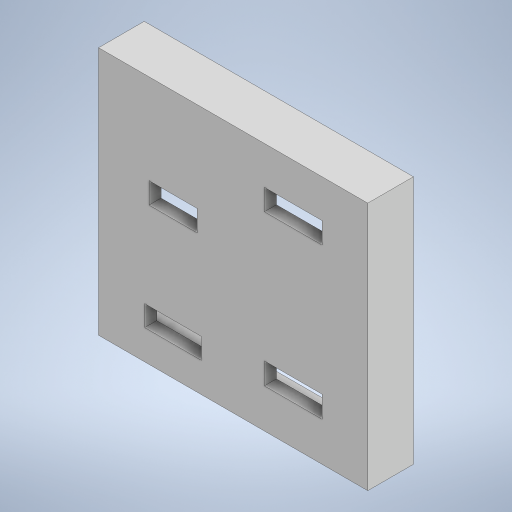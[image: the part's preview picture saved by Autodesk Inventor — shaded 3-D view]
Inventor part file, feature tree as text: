
AUTODESK INVENTOR PART (.ipt)
format: ipt  version: 2024 (Build 280153000, 153)  size: 269,312 bytes
history: native  units: in
note: dims shown in document units (in); Inventor stores cm internally (conversion verified against a paired STEP export)
features: sketch x2, extrude x2, projected_geometry x1
ambient origin geometry x8: Origin, YZ Plane, XZ Plane, XY Plane, X Axis, Y Axis, Z Axis, Center Point
bodies: Solid1 (feature_tree)
feature tree (5):
  sketch  "Sketch1"  dims[d0=0.02in d1=0.02in]
  extrude  "Extrusion1"  Depth=0.02in
  extrude  "Extrusion2"  Depth=0.125in
  sketch  "Sketch3"  dims[d2=0.125in d3=0.125in d4=0.125in d5=0.0in d6=0.125in d7=0.35in d8=0.0in d9=0.6in d10=0.22in d11=90.0deg d13=0.22in d14=0.22in d15=0.6in d16=0.6in d17=0.25in d18=0.225in]
  projected_geometry  "Projected Loop1"
